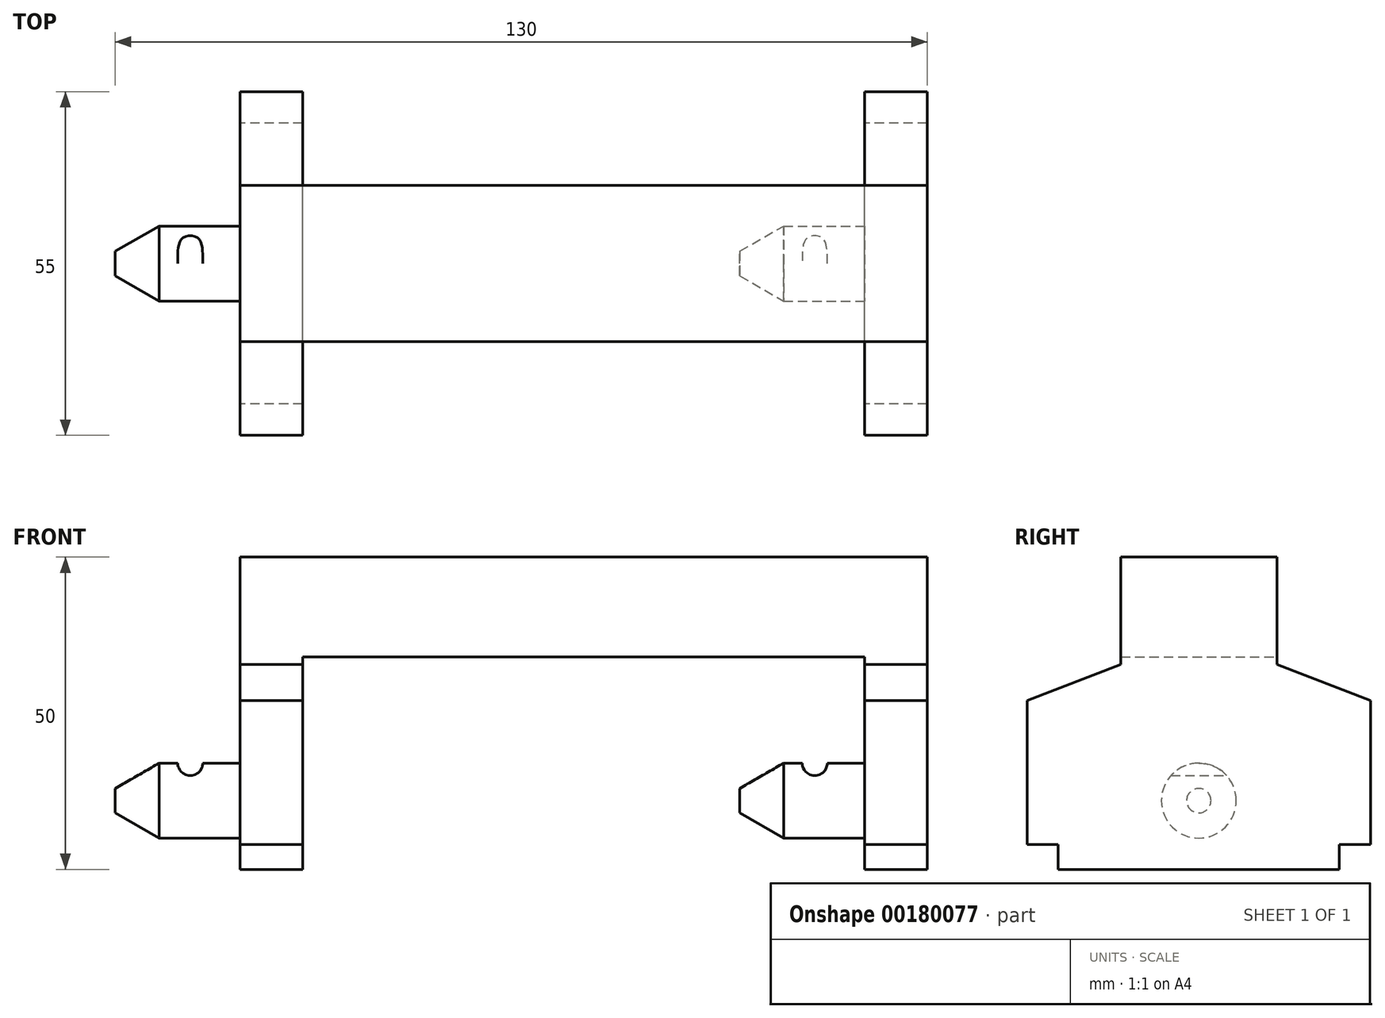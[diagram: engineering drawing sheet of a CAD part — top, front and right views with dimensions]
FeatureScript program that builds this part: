
annotation { "Feature Type Name" : "Feature", "Feature Type Description" : "" }
export const myFeature = defineFeature(function(context is Context, id is Id, definition is map)
    precondition{}
    {
        {
            var Q0;
            Q0=qCreatedBy(makeId("Front.planeOp"),FACE);
            var sketch = newSketch(context, id + "F0", { "sketchPlane" : qUnion([Q0])});
            skLineSegment(sketch, "E0", {"start": v(-45.46, 0) * mm, "end": v(-45.46, 50) * mm});
            skLineSegment(sketch, "E1", {"start": v(-45.46, 50) * mm, "end": v(64.54, 50) * mm});
            skLineSegment(sketch, "E2", {"start": v(64.54, 50) * mm, "end": v(64.54, 0) * mm});
            skLineSegment(sketch, "E3", {"start": v(64.54, 0) * mm, "end": v(54.54, 0) * mm});
            skLineSegment(sketch, "E4", {"start": v(54.54, 0) * mm, "end": v(54.54, 34) * mm});
            skLineSegment(sketch, "E5", {"start": v(54.54, 34) * mm, "end": v(-35.46, 34) * mm});
            skLineSegment(sketch, "E6", {"start": v(-35.46, 34) * mm, "end": v(-35.46, 0) * mm});
            skLineSegment(sketch, "E7", {"start": v(-35.46, 0) * mm, "end": v(-45.46, 0) * mm});
            skLineSegment(sketch, "E8", {"start": v(-68.34, 0) * mm, "end": v(58.07, 0) * mm, "construction": true});
            skSolve(sketch);
        }
        {
            var Q0;
            Q0 = qSketchRegion(id + "F0", true);
            extrude(context, id + "F1", {"entities" : qUnion([Q0]), "depth" : 55 * mm});
        }
        {
            var Q0;
            Q0=makeQuery(id+"F1.opExtrude","SWEPT_FACE",FACE,{"disambiguationData":[OSD([sQuery(id+"F0.wireOp",EDGE,"E0")])]});
            var sketch = newSketch(context, id + "F2", { "sketchPlane" : qUnion([Q0])});
            skLineSegment(sketch, "E9", {"start": v(0, 4) * mm, "end": v(5, 4) * mm});
            skLineSegment(sketch, "E10", {"start": v(5, 4) * mm, "end": v(5, 0) * mm});
            skLineSegment(sketch, "E11", {"start": v(50, 0) * mm, "end": v(50, 4) * mm});
            skLineSegment(sketch, "E12", {"start": v(50, 4) * mm, "end": v(55, 4) * mm});
            skSolve(sketch);
        }
        {
            var Q0;
            Q0 = qSketchRegion(id + "F2", true);
            var Q1;
            {var subQ0=sQuery(id+"F2.wireOp",EDGE,"E9");Q1=makeQuery(id+"F2.imprint","IMPRINT",FACE,{"disambiguationData":[TD([[makeQuery(id+"F2.imprint","IMPRINT",EDGE,{"derivedFrom":subQ0}),-1.0]])]});}
            var Q2;
            {var subQ0=sQuery(id+"F2.wireOp",EDGE,"E11");Q2=makeQuery(id+"F2.imprint","IMPRINT",FACE,{"disambiguationData":[TD([[makeQuery(id+"F2.imprint","IMPRINT",EDGE,{"derivedFrom":subQ0}),-1.0]])]});}
            extrude(context, id + "F3", {"entities" : qUnion([Q0, Q1, Q2]), "operationType" : NewBodyOperationType.REMOVE, "endBound" : BoundingType.THROUGH_ALL, "oppositeDirection" : true, "depth" : 25 * mm});
        }
        {
            var Q0;
            Q0=makeQuery(id+"F1.opExtrude","SWEPT_FACE",FACE,{"disambiguationData":[OSD([sQuery(id+"F0.wireOp",EDGE,"E0")])]});
            var sketch = newSketch(context, id + "F4", { "sketchPlane" : qUnion([Q0])});
            skLineSegment(sketch, "E13", {"start": v(0, 11) * mm, "end": v(55, 11) * mm, "construction": true});
            skLineSegment(sketch, "E14", {"start": v(27.5, 0) * mm, "end": v(27.5, 50) * mm, "construction": true});
            skCircle(sketch, "E15", {"center": v(27.5, 11) * mm, "radius": 6 * mm});
            skSolve(sketch);
        }
        {
            var Q0;
            Q0 = qSketchRegion(id + "F4", true);
            extrude(context, id + "F5", {"entities" : qUnion([Q0]), "operationType" : NewBodyOperationType.ADD, "depth" : 20 * mm});
        }
        {
            var Q0;
            Q0=makeQuery(id+"F1.opExtrude","SWEPT_FACE",FACE,{"disambiguationData":[OSD([sQuery(id+"F0.wireOp",EDGE,"E4")])]});
            var sketch = newSketch(context, id + "F6", { "sketchPlane" : qUnion([Q0])});
            skLineSegment(sketch, "E16", {"start": v(0, 11) * mm, "end": v(55, 11) * mm, "construction": true});
            skLineSegment(sketch, "E17", {"start": v(27.5, 0) * mm, "end": v(27.5, 34) * mm, "construction": true});
            skCircle(sketch, "E18", {"center": v(27.5, 11) * mm, "radius": 6 * mm});
            skSolve(sketch);
        }
        {
            var Q0;
            Q0 = qSketchRegion(id + "F6", true);
            extrude(context, id + "F7", {"entities" : qUnion([Q0]), "operationType" : NewBodyOperationType.ADD, "depth" : 20 * mm});
        }
        {
            var Q0;
            Q0=makeQuery(id+"F1.opExtrude","SWEPT_FACE",FACE,{"disambiguationData":[OSD([sQuery(id+"F0.wireOp",EDGE,"E0")])]});
            var sketch = newSketch(context, id + "F8", { "sketchPlane" : qUnion([Q0])});
            skLineSegment(sketch, "E19", {"start": v(55, 27) * mm, "end": v(40, 32.83) * mm});
            skLineSegment(sketch, "E20", {"start": v(40, 32.83) * mm, "end": v(40, 50) * mm});
            skLineSegment(sketch, "E21", {"start": v(0, 27) * mm, "end": v(15, 32.83) * mm});
            skLineSegment(sketch, "E22", {"start": v(15, 32.83) * mm, "end": v(15, 50) * mm});
            skLineSegment(sketch, "E23", {"start": v(0, 27) * mm, "end": v(0, 50) * mm});
            skLineSegment(sketch, "E24", {"start": v(0, 50) * mm, "end": v(15, 50) * mm});
            skLineSegment(sketch, "E25", {"start": v(40, 50) * mm, "end": v(55, 50) * mm});
            skLineSegment(sketch, "E26", {"start": v(55, 50) * mm, "end": v(55, 27) * mm});
            skSolve(sketch);
        }
        {
            var Q0;
            Q0=makeQuery(id+"F8.imprint","IMPRINT",FACE,{"disambiguationData":[TD([[makeQuery(id+"F8.imprint","IMPRINT",EDGE,{"derivedFrom":sQuery(id+"F8.wireOp",EDGE,"E19")}),-1.0]])]});
            var Q1;
            Q1=makeQuery(id+"F8.imprint","IMPRINT",FACE,{"disambiguationData":[TD([[makeQuery(id+"F8.imprint","IMPRINT",EDGE,{"derivedFrom":sQuery(id+"F8.wireOp",EDGE,"E21")}),1.0]])]});
            extrude(context, id + "F9", {"entities" : qUnion([Q0, Q1]), "operationType" : NewBodyOperationType.REMOVE, "endBound" : BoundingType.THROUGH_ALL, "oppositeDirection" : true, "depth" : 25 * mm});
        }
        {
            var Q0;
            Q0=makeQuery(id+"F5.opExtrude","CAP_FACE",FACE,{"disambiguationData":[OSD([sQuery(id+"F4.wireOp",EDGE,"E15")])],"isStart":false});
            var Q1;
            Q1=makeQuery(id+"F7.opExtrude","CAP_FACE",FACE,{"disambiguationData":[OSD([sQuery(id+"F6.wireOp",EDGE,"E18")])],"isStart":false});
            chamfer(context, id + "F10", {"entities" : qUnion([Q0, Q1]), "chamferType" : ChamferType.OFFSET_ANGLE, "width" : 7 * mm, "oppositeDirection" : true, "angle" : 30 * degree, "tangentPropagation" : true});
        }
        {
            var Q0;
            Q0=qCreatedBy(makeId("Front.planeOp"),FACE);
            var sketch = newSketch(context, id + "F11", { "sketchPlane" : qUnion([Q0])});
            skCircle(sketch, "E27", {"center": v(-53.46, 17) * mm, "radius": 2 * mm});
            skCircle(sketch, "E28", {"center": v(46.54, 17) * mm, "radius": 2 * mm});
            skSolve(sketch);
        }
        {
            var Q0;
            Q0 = qSketchRegion(id + "F11", true);
            extrude(context, id + "F12", {"entities" : qUnion([Q0]), "operationType" : NewBodyOperationType.REMOVE, "endBound" : BoundingType.THROUGH_ALL, "depth" : 25 * mm});
        }
    });
